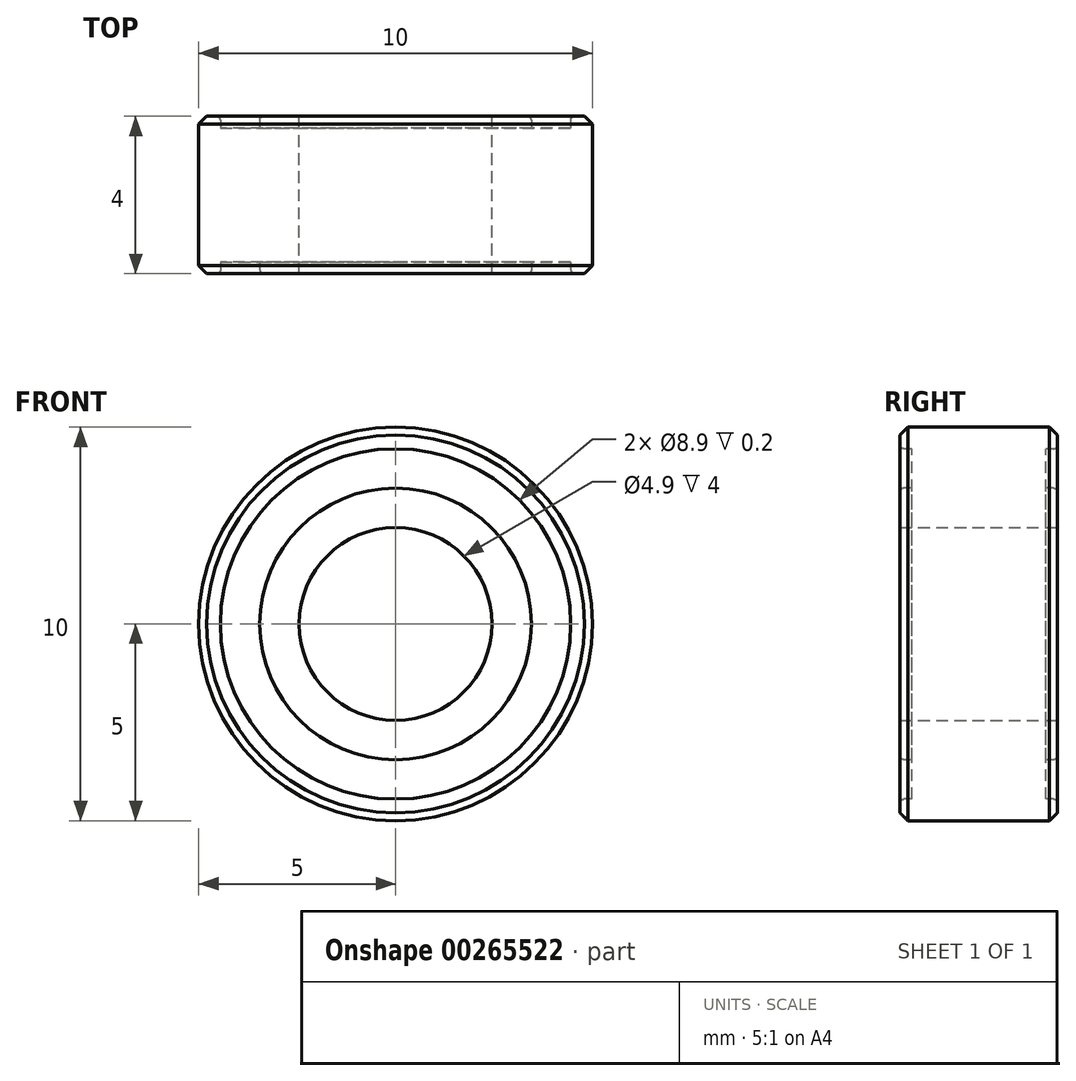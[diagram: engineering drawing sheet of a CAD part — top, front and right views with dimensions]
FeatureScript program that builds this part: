
annotation { "Feature Type Name" : "Feature", "Feature Type Description" : "" }
export const myFeature = defineFeature(function(context is Context, id is Id, definition is map)
    precondition{}
    {
        {
            var Q0;
            Q0=qCreatedBy(makeId("Front.planeOp"),FACE);
            var sketch = newSketch(context, id + "F0", { "sketchPlane" : qUnion([Q0])});
            skCircle(sketch, "E0", {"center": v(0, 0) * mm, "radius": 5 * mm});
            skCircle(sketch, "E1", {"center": v(0, 0) * mm, "radius": 2.45 * mm});
            skSolve(sketch);
        }
        {
            var Q0;
            Q0=makeQuery(id+"F0.imprint","IMPRINT",FACE,{"disambiguationData":[TD([[makeQuery(id+"F0.imprint","IMPRINT",EDGE,{"derivedFrom":sQuery(id+"F0.wireOp",EDGE,"E0")}),1.0]])]});
            extrude(context, id + "F1", {"entities" : qUnion([Q0]), "depth" : 4 * mm});
        }
        {
            var Q0;
            Q0=qCreatedBy(makeId("Right.planeOp"),FACE);
            var sketch = newSketch(context, id + "F2", { "sketchPlane" : qUnion([Q0])});
            skLineSegment(sketch, "E2", {"start": v(0, 0) * mm, "end": v(-11.08, 0) * mm, "construction": true});
            skSolve(sketch);
        }
        {
            var Q0;
            Q0=qCreatedBy(makeId("Top.planeOp"),FACE);
            var sketch = newSketch(context, id + "F3", { "sketchPlane" : qUnion([Q0])});
            skLineSegment(sketch, "E3", {"start": v(0, 0) * mm, "end": v(-3.45, 0) * mm, "construction": true});
            skLineSegment(sketch, "E4", {"start": v(-3.45, 0) * mm, "end": v(-3.45, -0.3) * mm, "construction": true});
            skLineSegment(sketch, "E5.bottom", {"start": v(-3.45, -0.3) * mm, "end": v(-4.45, -0.3) * mm});
            skLineSegment(sketch, "E5.top", {"start": v(-3.45, 0.7) * mm, "end": v(-4.45, 0.7) * mm});
            skLineSegment(sketch, "E5.left", {"start": v(-3.45, -0.3) * mm, "end": v(-3.45, 0.7) * mm});
            skLineSegment(sketch, "E5.right", {"start": v(-4.45, -0.3) * mm, "end": v(-4.45, 0.7) * mm});
            skLineSegment(sketch, "E6", {"start": v(0, 0) * mm, "end": v(0, -4) * mm, "construction": true});
            skLineSegment(sketch, "E7", {"start": v(0, -4) * mm, "end": v(-3.45, -4) * mm, "construction": true});
            skLineSegment(sketch, "E8", {"start": v(-3.45, -4) * mm, "end": v(-3.45, -3.7) * mm, "construction": true});
            skLineSegment(sketch, "E9.bottom", {"start": v(-3.45, -3.7) * mm, "end": v(-4.45, -3.7) * mm});
            skLineSegment(sketch, "E9.top", {"start": v(-3.45, -4.7) * mm, "end": v(-4.45, -4.7) * mm});
            skLineSegment(sketch, "E9.left", {"start": v(-3.45, -3.7) * mm, "end": v(-3.45, -4.7) * mm});
            skLineSegment(sketch, "E9.right", {"start": v(-4.45, -3.7) * mm, "end": v(-4.45, -4.7) * mm});
            skSolve(sketch);
        }
        {
            var Q0;
            Q0=makeQuery(id+"F3.imprint","IMPRINT",FACE,{"disambiguationData":[TD([[makeQuery(id+"F3.imprint","IMPRINT",EDGE,{"derivedFrom":sQuery(id+"F3.wireOp",EDGE,"E5.bottom")}),-1.0]])]});
            var Q1;
            Q1=makeQuery(id+"F3.imprint","IMPRINT",FACE,{"disambiguationData":[TD([[makeQuery(id+"F3.imprint","IMPRINT",EDGE,{"derivedFrom":sQuery(id+"F3.wireOp",EDGE,"E9.bottom")}),1.0]])]});
            var Q2;
            Q2=sQuery(id+"F2.wireOp",EDGE,"E2");
            revolve(context, id + "F4", {"operationType" : NewBodyOperationType.REMOVE, "entities" : qUnion([Q0, Q1]), "axis" : qUnion([Q2]), "revolveType" : RevolveType.FULL, "oppositeDirection" : true});
        }
        {
            var Q0;
            Q0=makeQuery(id+"F4.boolean.opBoolean","INTERSECT",EDGE,{"derivedFrom":[makeQuery(id+"F1.opExtrude","CAP_FACE",FACE,{"disambiguationData":[OSD([sQuery(id+"F0.wireOp",EDGE,"E0"),sQuery(id+"F0.wireOp",EDGE,"E1")])],"isStart":true}),makeQuery(id+"F4.opRevolve","SWEPT_FACE",FACE,{"disambiguationData":[OSD([sQuery(id+"F3.wireOp",EDGE,"E5.right")])]})]});
            var Q1;
            Q1=makeQuery(id+"F4.boolean.opBoolean","INTERSECT",EDGE,{"derivedFrom":[makeQuery(id+"F1.opExtrude","CAP_FACE",FACE,{"disambiguationData":[OSD([sQuery(id+"F0.wireOp",EDGE,"E0"),sQuery(id+"F0.wireOp",EDGE,"E1")])],"isStart":true}),makeQuery(id+"F4.opRevolve","SWEPT_FACE",FACE,{"disambiguationData":[OSD([sQuery(id+"F3.wireOp",EDGE,"E5.left")])]})]});
            var Q2;
            Q2=makeQuery(id+"F4.boolean.opBoolean","INTERSECT",EDGE,{"derivedFrom":[makeQuery(id+"F1.opExtrude","CAP_FACE",FACE,{"disambiguationData":[OSD([sQuery(id+"F0.wireOp",EDGE,"E0"),sQuery(id+"F0.wireOp",EDGE,"E1")])],"isStart":false}),makeQuery(id+"F4.opRevolve","SWEPT_FACE",FACE,{"disambiguationData":[OSD([sQuery(id+"F3.wireOp",EDGE,"E9.right")])]})]});
            var Q3;
            Q3=makeQuery(id+"F4.boolean.opBoolean","INTERSECT",EDGE,{"derivedFrom":[makeQuery(id+"F1.opExtrude","CAP_FACE",FACE,{"disambiguationData":[OSD([sQuery(id+"F0.wireOp",EDGE,"E0"),sQuery(id+"F0.wireOp",EDGE,"E1")])],"isStart":false}),makeQuery(id+"F4.opRevolve","SWEPT_FACE",FACE,{"disambiguationData":[OSD([sQuery(id+"F3.wireOp",EDGE,"E9.left")])]})]});
            fillet(context, id + "F5", {"entities" : qUnion([Q0, Q1, Q2, Q3]), "radius" : 0.1 * mm, "tangentPropagation" : true, "allowEdgeOverflow" : false});
        }
        {
            var Q0;
            Q0=makeQuery(id+"F1.opExtrude","CAP_EDGE",EDGE,{"disambiguationData":[OSD([sQuery(id+"F0.wireOp",EDGE,"E0")])],"isStart":false});
            var Q1;
            Q1=makeQuery(id+"F1.opExtrude","CAP_EDGE",EDGE,{"disambiguationData":[OSD([sQuery(id+"F0.wireOp",EDGE,"E0")])],"isStart":true});
            chamfer(context, id + "F6", {"entities" : qUnion([Q0, Q1]), "width" : 0.2 * mm, "tangentPropagation" : true});
        }
    });
